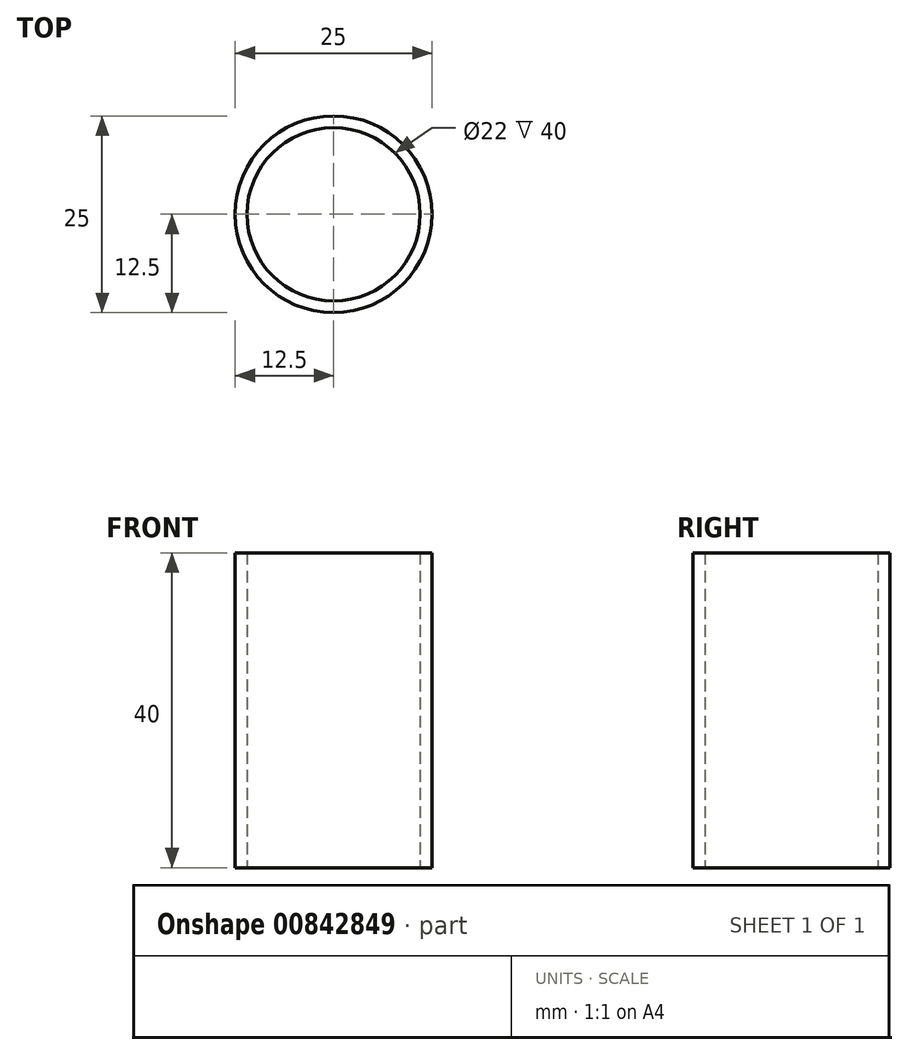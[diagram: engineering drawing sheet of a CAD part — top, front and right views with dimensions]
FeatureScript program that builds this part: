
annotation { "Feature Type Name" : "Feature", "Feature Type Description" : "" }
export const myFeature = defineFeature(function(context is Context, id is Id, definition is map)
    precondition{}
    {
        {
            var Q0;
            Q0=qCreatedBy(makeId("Top.planeOp"),FACE);
            var sketch = newSketch(context, id + "F0", { "sketchPlane" : qUnion([Q0])});
            skCircle(sketch, "E0", {"center": v(0, 0) * mm, "radius": 12.5 * mm});
            skCircle(sketch, "E1", {"center": v(0, 0) * mm, "radius": 11 * mm});
            skSolve(sketch);
        }
        {
            var Q0;
            Q0=makeQuery(id+"F0.imprint","IMPRINT",FACE,{"disambiguationData":[TD([[makeQuery(id+"F0.imprint","IMPRINT",EDGE,{"derivedFrom":sQuery(id+"F0.wireOp",EDGE,"E0")}),1.0]])]});
            extrude(context, id + "F1", {"entities" : qUnion([Q0]), "depth" : 40 * mm, "offsetDistance" : 25 * mm});
        }
    });
